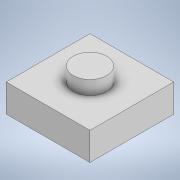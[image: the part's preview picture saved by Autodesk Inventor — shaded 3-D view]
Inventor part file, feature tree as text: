
AUTODESK INVENTOR PART (.ipt)
format: ipt  version: 2020 (Build 240168000, 168)  size: 99,840 bytes
history: native  units: in
note: dims shown in document units (in); Inventor stores cm internally (conversion verified against a paired STEP export)
features: extrude x2, sketch x2
ambient origin geometry x8: Origin, YZ Plane, XZ Plane, XY Plane, X Axis, Y Axis, Z Axis, Center Point
bodies: Solid1 (feature_tree)
feature tree (4):
  extrude  "Extrusion1"  Depth=0.75in
  extrude  "Extrusion2"  Depth=0.125in
  sketch  "Sketch1"  dims[d0=0.75in d1=0.75in]
  sketch  "Sketch2"  dims[d2=0.25in d3=0.0in d4=0.3in d5=0.125in d6=0.0in]
